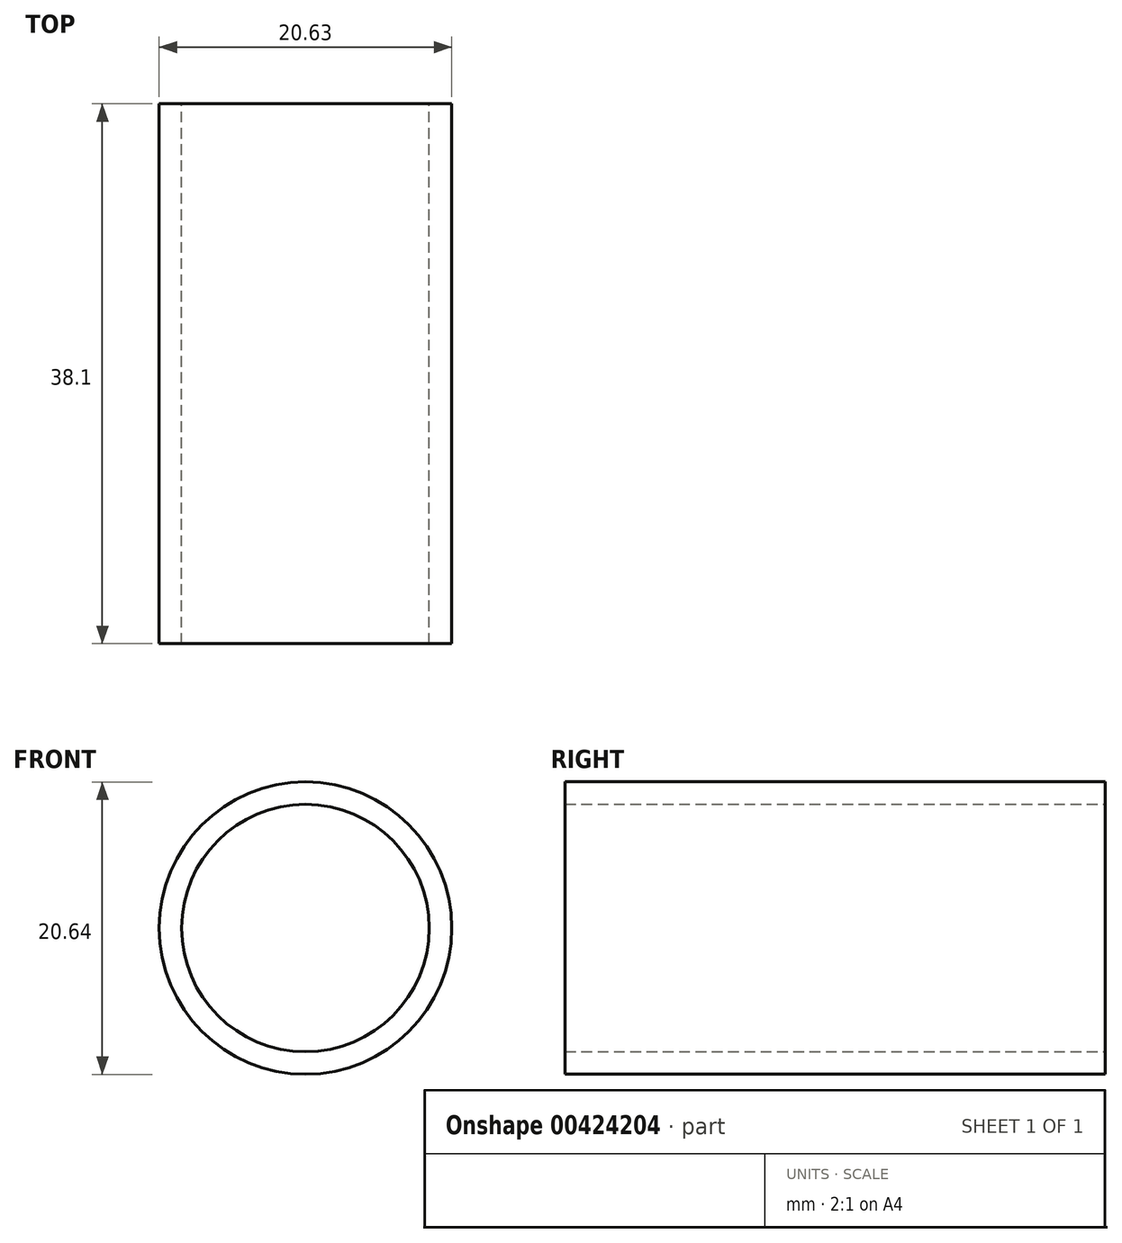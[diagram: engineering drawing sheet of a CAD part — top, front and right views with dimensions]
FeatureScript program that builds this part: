
annotation { "Feature Type Name" : "Feature", "Feature Type Description" : "" }
export const myFeature = defineFeature(function(context is Context, id is Id, definition is map)
    precondition{}
    {
        {
            var Q0;
            Q0=qCreatedBy(makeId("Front.planeOp"),FACE);
            var sketch = newSketch(context, id + "F0", { "sketchPlane" : qUnion([Q0])});
            skCircle(sketch, "E0", {"center": v(0.78, 1.3) * mm, "radius": 10.32 * mm});
            skCircle(sketch, "E1", {"center": v(0.78, 1.3) * mm, "radius": 8.73 * mm});
            skSolve(sketch);
        }
        {
            var Q0;
            Q0=qSketchRegion(id+"F0",true);
            extrude(context, id + "F1", {"entities" : qUnion([Q0]), "depth" : 38.1 * mm});
        }
    });
